# Revit family: lgh-rn150_200rxv2d-c_50Hz
name_source: partatom
category: 機械設備
units: mm (PartAtom-declared; Revit-internal decimal feet)

## family parameters
OmniClass タイトル = Heat Exchangers for Ventilation Air
OmniClass 番号 = 23.75.10.34.21
パーツ タイプ = 割り込み
ロード時にボイドで切り取り = いいえ
丸型コネクタ寸法 = 直径を使用
作業面ベース = いいえ
共有 = いいえ
常に垂直 = はい
部屋計算ポイント = はい

## types (2) — shared parameters
Clearance Left = 600
Depth = 1144  [stored 3.75328 ft]
EAサイズ_D = 700  [stored 2.29659 ft]
EAサイズ_W = 270  [stored 0.885827 ft]
Height = 808  [stored 2.65092 ft]
IfcExportAs = IfcAirToAirHeatRecoveryType
IfcExportType = ROTARYWHEEL
M1 = 84  [stored 0.275591 ft]
M2 = 49  [stored 0.160761 ft]
OAサイズ_D = 700  [stored 2.29659 ft]
OAサイズ_W = 270  [stored 0.885827 ft]
OmniClassCode = 23-27 23 19 11
RAサイズ_D = 242  [stored 0.793963 ft]
SAサイズ_D = 242  [stored 0.793963 ft]
URL = https://www.mitsubishielectric.co.jp
Uniclass2015Code = Pr_60_60_36_88
Uniclass2015Title = Thermal wheels
Uniclass2015Version = Systems v1.9
サービススペース = はい
ダクト幅 = 270 mm
ダクト径 = 250 mm
ダクト高 = 700 mm
仕様書バージョン = Version1.0
企業コード = 108420
分類コード = 50052504100070
初期抵抗 = 0.0 Pa
吊りボルト-D = 1030  [stored 3.37927 ft]
周波数 = 50 Hz
呼称 = 全熱交換ユニット
外気量 = 0.0 m³/h
実風量 = 0.0 m³/h
形名 = LGH-RN-3 : LGH-RN150-3
形式 = 天井埋込ダクト形
排気量 = 0.0 m³/h
本体マテリアル = 溶融亜鉛めっき鋼板
極数 = 3
法定耐用年数 = 15
点検口 = はい
点検口高さ = -404  [stored -1.32546 ft]
相 = 1
積算_科目 = 1 空気調和設備
製品リリース年月 = 2023/5/15
製品出荷対象 = 国内
製造元 = 三菱電機株式会社
設置方法 = 天井吊(隠ぺい)形
設計風量 = 0.0 m³/h
説明 = 業務用ロスナイ 天井埋込形 DCリプレースマイコン CO2センサー付
負荷分類 = 3_ファン類
運転質量 = 0.00 kg
電動機出力 = 0 W
電圧 = 200 V
zero-valued in all types: Clearance Back, Clearance Bottom, Clearance Front, Clearance Right, Clearance Top

## per-type parameters (varying)
- LGH-RN150RXV2D-C: MAX静圧=245.0 Pa; MAX風量=1500.0 m³/h; MID静圧=127.0 Pa; MID風量=1080.0 m³/h; MIN静圧=47.0 Pa; MIN風量=660.0 m³/h; SMAX静圧=275.0 Pa; SMAX風量=1500.0 m³/h; Width=1004  [stored 3.29396 ft]; エンタルピ交換効率_冷房_弱=68.50%; エンタルピ交換効率_冷房_強=66.00%; エンタルピ交換効率_冷房_特強=66.00%; エンタルピ交換効率_暖房_弱=78.50%; エンタルピ交換効率_暖房_強=76.00%; エンタルピ交換効率_暖房_特強=76.00%; 価格=1441200 $; 吊りボルト-W=1046  [stored 3.43176 ft]; 機外静圧=275.0 Pa; 機外静圧_排気=275.0 Pa; 消費電力=900 W; 温度交換効率_弱=76.50%; 温度交換効率_強=74.00%; 温度交換効率_特強=74.00%; 製品質量=107.00 kg; 質量=128.40 kg; 面風速=8.5 m/s; 風量=1500.0 m³/h; 騒音レベル(dB(A))=38.5
- LGH-RN200RXV2D-C: MAX静圧=165.0 Pa; MAX風量=2000.0 m³/h; MID静圧=86.0 Pa; MID風量=1440.0 m³/h; MIN静圧=32.0 Pa; MIN風量=880.0 m³/h; SMAX静圧=225.0 Pa; SMAX風量=2000.0 m³/h; Width=1231  [stored 4.03871 ft]; エンタルピ交換効率_冷房_弱=67.50%; エンタルピ交換効率_冷房_強=65.00%; エンタルピ交換効率_冷房_特強=65.00%; エンタルピ交換効率_暖房_弱=76.50%; エンタルピ交換効率_暖房_強=75.00%; エンタルピ交換効率_暖房_特強=75.00%; 価格=1614200 $; 吊りボルト-W=1273  [stored 4.17651 ft]; 機外静圧=225.0 Pa; 機外静圧_排気=225.0 Pa; 消費電力=1160 W; 温度交換効率_弱=75.00%; 温度交換効率_強=73.00%; 温度交換効率_特強=73.00%; 製品質量=117.00 kg; 質量=140.40 kg; 面風速=11.3 m/s; 風量=2000.0 m³/h; 騒音レベル(dB(A))=41

note: column(s) folded — value = type name in every type: モデル

note: [stored X ft] marks values corroborated as IEEE doubles in the binary element streams (Revit-internal decimal feet)
